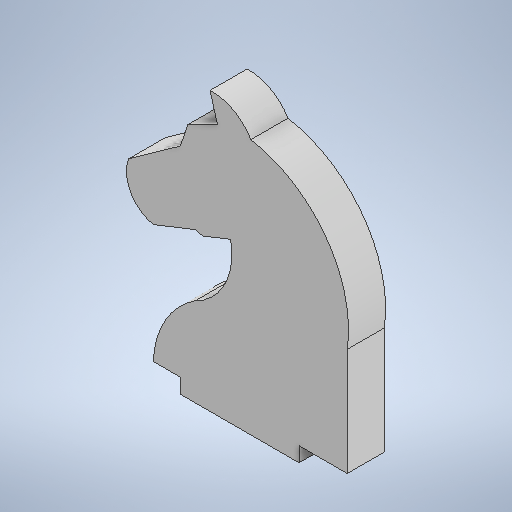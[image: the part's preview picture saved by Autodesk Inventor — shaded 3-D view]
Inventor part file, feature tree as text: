
AUTODESK INVENTOR PART (.ipt)
format: ipt  version: 2025.1 (Build 291241000, 241)  size: 288,768 bytes
history: native  units: mm
features: other x2, extrude x1, sketch x1
ambient origin geometry x8: Origin, YZ Plane, XZ Plane, XY Plane, X Axis, Y Axis, Z Axis, Center Point
bodies: Body1 (feature_tree)
feature tree (4):
  other  "Sólido1"
  extrude  "Extrusión1"  [1 undecoded]
  sketch  "Boceto1"  dims[d5=10.0mm d6=0.0mm]
  other  "Imagen1"
note: 1 required parameter value undecoded (feature->parameter linkage not recoverable at this tier; creation-order binding heuristic only, values carry confidence <= 0.55)
